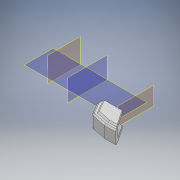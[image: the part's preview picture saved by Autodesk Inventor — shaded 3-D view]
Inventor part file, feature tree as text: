
AUTODESK INVENTOR PART (.ipt)
format: ipt  version: 2018 (Build 220112000, 112)  size: 1,472,512 bytes
history: native  units: mm
features: other x8, extrude x1, sketch x1
ambient origin geometry x8: Origin, YZ Plane, XZ Plane, XY Plane, X Axis, Y Axis, Z Axis, Center Point
bodies: Body1 (feature_tree)
feature tree (10):
  other  "undercover.ipt"
  extrude  "押し出し1"  Depth=10.0mm
  other  "ソリッド1::undercover.ipt"
  other  "TaggingFeature1"
  other  "作業平面1"
  other  "作業平面2"
  other  "作業平面3"
  other  "作業平面4"
  sketch  "スケッチ1"
  other  "ソリッド1"
